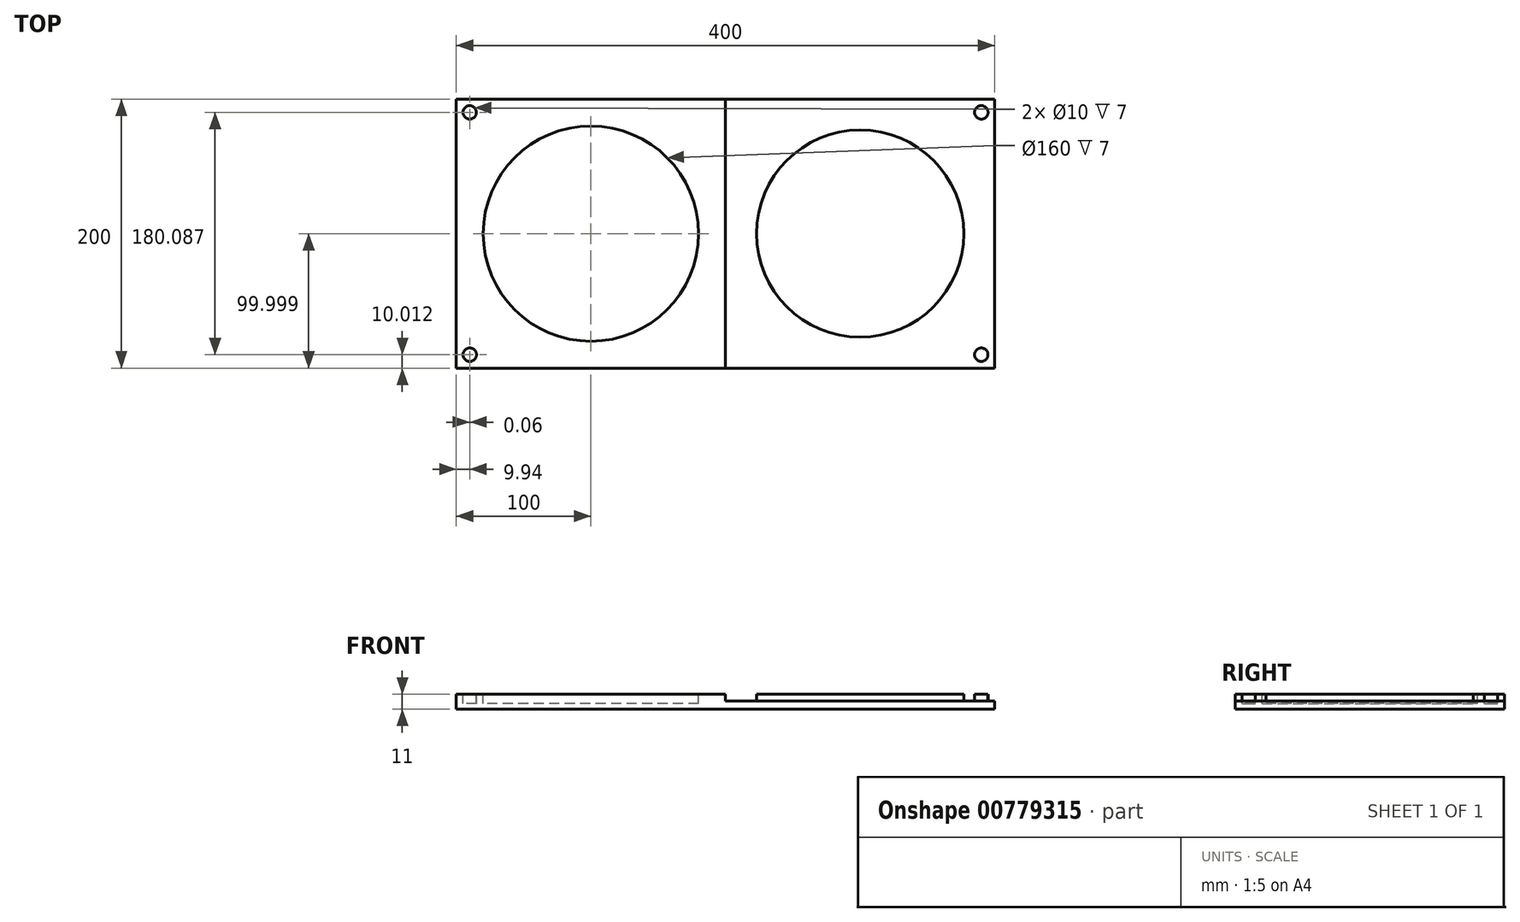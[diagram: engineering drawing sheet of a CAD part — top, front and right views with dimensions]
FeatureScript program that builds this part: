
annotation { "Feature Type Name" : "Feature", "Feature Type Description" : "" }
export const myFeature = defineFeature(function(context is Context, id is Id, definition is map)
    precondition{}
    {
        {
            var Q0;
            Q0=qCreatedBy(makeId("Top.planeOp"),FACE);
            var sketch = newSketch(context, id + "F0", { "sketchPlane" : qUnion([Q0])});
            skLineSegment(sketch, "E0.bottom", {"start": v(-35.15, 181.43) * mm, "end": v(364.85, 181.43) * mm});
            skLineSegment(sketch, "E0.top", {"start": v(-35.15, -18.57) * mm, "end": v(364.85, -18.57) * mm});
            skLineSegment(sketch, "E0.left", {"start": v(-35.15, 181.43) * mm, "end": v(-35.15, -18.57) * mm});
            skLineSegment(sketch, "E0.right", {"start": v(364.85, 181.43) * mm, "end": v(364.85, -18.57) * mm});
            skSolve(sketch);
        }
        {
            var Q0;
            Q0=makeQuery(id+"F0.imprint","IMPRINT",FACE,{"disambiguationData":[TD([[makeQuery(id+"F0.imprint","IMPRINT",EDGE,{"derivedFrom":sQuery(id+"F0.wireOp",EDGE,"E0.bottom")}),-1.0]])]});
            extrude(context, id + "F1", {"entities" : qUnion([Q0]), "depth" : 11 * mm, "offsetDistance" : 25 * mm});
        }
        {
            var Q0;
            Q0=makeQuery(id+"F1.opExtrude","CAP_FACE",FACE,{"disambiguationData":[OSD([sQuery(id+"F0.wireOp",EDGE,"E0.bottom"),sQuery(id+"F0.wireOp",EDGE,"E0.top"),sQuery(id+"F0.wireOp",EDGE,"E0.left"),sQuery(id+"F0.wireOp",EDGE,"E0.right")])],"isStart":false});
            var sketch = newSketch(context, id + "F2", { "sketchPlane" : qUnion([Q0])});
            skLineSegment(sketch, "E1", {"start": v(164.85, 181.43) * mm, "end": v(164.85, -18.57) * mm});
            skLineSegment(sketch, "E2", {"start": v(164.85, 81.43) * mm, "end": v(364.85, 81.43) * mm, "construction": true});
            skLineSegment(sketch, "E3", {"start": v(164.85, 81.43) * mm, "end": v(-35.15, 81.43) * mm, "construction": true});
            skCircle(sketch, "E4", {"center": v(64.85, 81.43) * mm, "radius": 80 * mm});
            skCircle(sketch, "E5", {"center": v(264.85, 81.43) * mm, "radius": 77 * mm});
            skLineSegment(sketch, "E6.0", {"start": v(-25.15, 181.43) * mm, "end": v(-25.15, -18.57) * mm, "construction": true});
            skLineSegment(sketch, "E7.0", {"start": v(-35.15, 171.43) * mm, "end": v(364.85, 171.43) * mm, "construction": true});
            skLineSegment(sketch, "E8.0", {"start": v(-35.15, -8.57) * mm, "end": v(364.85, -8.57) * mm, "construction": true});
            skCircle(sketch, "E9", {"center": v(-25.2, 171.53) * mm, "radius": 5 * mm});
            skCircle(sketch, "E10", {"center": v(-25.15, -8.56) * mm, "radius": 5 * mm});
            skCircle(sketch, "E11.MirrorC", {"center": v(354.85, -8.56) * mm, "radius": 5 * mm});
            skCircle(sketch, "E12.MirrorC", {"center": v(354.9, 171.53) * mm, "radius": 5 * mm});
            skSolve(sketch);
        }
        {
            var Q0;
            Q0=makeQuery(id+"F2.imprint","IMPRINT",FACE,{"disambiguationData":[TD([[makeQuery(id+"F2.imprint","IMPRINT",EDGE,{"derivedFrom":sQuery(id+"F2.wireOp",EDGE,"E10")}),1.0]])]});
            var Q1;
            Q1=makeQuery(id+"F2.imprint","IMPRINT",FACE,{"disambiguationData":[TD([[makeQuery(id+"F2.imprint","IMPRINT",EDGE,{"derivedFrom":sQuery(id+"F2.wireOp",EDGE,"E4")}),1.0]])]});
            var Q2;
            Q2=makeQuery(id+"F2.imprint","IMPRINT",FACE,{"disambiguationData":[TD([[makeQuery(id+"F2.imprint","IMPRINT",EDGE,{"derivedFrom":sQuery(id+"F2.wireOp",EDGE,"E9")}),1.0]])]});
            extrude(context, id + "F3", {"entities" : qUnion([Q0, Q1, Q2]), "operationType" : NewBodyOperationType.REMOVE, "oppositeDirection" : true, "depth" : 7 * mm, "offsetDistance" : 25 * mm});
        }
        {
            var Q0;
            {var subQ2=sQuery(id+"F2.wireOp",EDGE,"E1");Q0=makeQuery(id+"F2.imprint","IMPRINT",FACE,{"disambiguationData":[TD([[makeQuery(id+"F2.imprint","IMPRINT",EDGE,{"derivedFrom":subQ2}),1.0]])]});}
            extrude(context, id + "F4", {"entities" : qUnion([Q0]), "operationType" : NewBodyOperationType.REMOVE, "oppositeDirection" : true, "depth" : 5 * mm, "offsetDistance" : 25 * mm});
        }
    });
